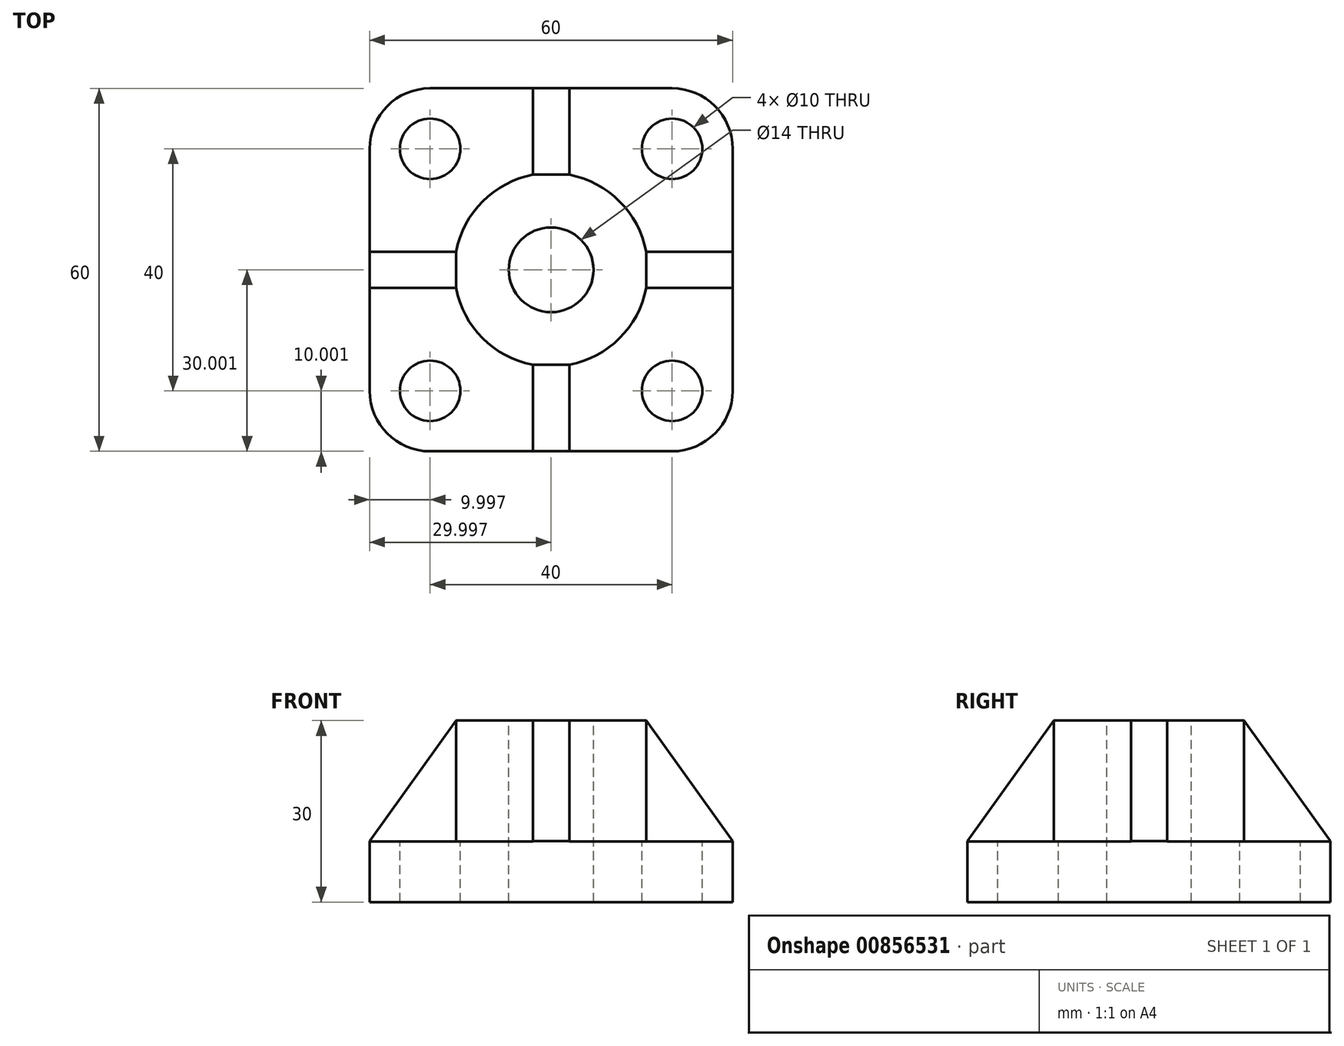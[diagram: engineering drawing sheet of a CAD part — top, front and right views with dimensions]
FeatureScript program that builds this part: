
annotation { "Feature Type Name" : "Feature", "Feature Type Description" : "" }
export const myFeature = defineFeature(function(context is Context, id is Id, definition is map)
    precondition{}
    {
        {
            var Q0;
            Q0=qCreatedBy(makeId("Top.planeOp"),FACE);
            var sketch = newSketch(context, id + "F0", { "sketchPlane" : qUnion([Q0])});
            skLineSegment(sketch, "E0.bottom", {"start": v(-13.96, 23.61) * mm, "end": v(46.04, 23.61) * mm});
            skLineSegment(sketch, "E0.top", {"start": v(-13.96, -36.39) * mm, "end": v(46.04, -36.39) * mm});
            skLineSegment(sketch, "E0.left", {"start": v(-13.96, 23.61) * mm, "end": v(-13.96, -36.39) * mm});
            skLineSegment(sketch, "E0.right", {"start": v(46.04, 23.61) * mm, "end": v(46.04, -36.39) * mm});
            skSolve(sketch);
        }
        {
            var Q0;
            Q0=makeQuery(id+"F0.imprint","IMPRINT",FACE,{"disambiguationData":[TD([[makeQuery(id+"F0.imprint","IMPRINT",EDGE,{"derivedFrom":sQuery(id+"F0.wireOp",EDGE,"E0.bottom")}),-1.0]])]});
            extrude(context, id + "F1", {"entities" : qUnion([Q0]), "depth" : 10 * mm, "offsetDistance" : 25 * mm});
        }
        {
            var Q0;
            Q0=makeQuery(id+"F1.opExtrude","SWEPT_EDGE",EDGE,{"disambiguationData":[OSD([sQuery(id+"F0.wireOp",EDGE,"E0.bottom"),sQuery(id+"F0.wireOp",EDGE,"E0.left")])]});
            var Q1;
            Q1=makeQuery(id+"F1.opExtrude","SWEPT_EDGE",EDGE,{"disambiguationData":[OSD([sQuery(id+"F0.wireOp",EDGE,"E0.bottom"),sQuery(id+"F0.wireOp",EDGE,"E0.right")])]});
            var Q2;
            Q2=makeQuery(id+"F1.opExtrude","SWEPT_EDGE",EDGE,{"disambiguationData":[OSD([sQuery(id+"F0.wireOp",EDGE,"E0.top"),sQuery(id+"F0.wireOp",EDGE,"E0.right")])]});
            var Q3;
            Q3=makeQuery(id+"F1.opExtrude","SWEPT_EDGE",EDGE,{"disambiguationData":[OSD([sQuery(id+"F0.wireOp",EDGE,"E0.top"),sQuery(id+"F0.wireOp",EDGE,"E0.left")])]});
            fillet(context, id + "F2", {"entities" : qUnion([Q0, Q1, Q2, Q3]), "radius" : 10 * mm, "tangentPropagation" : true, "allowEdgeOverflow" : false});
        }
        {
            var Q0;
            Q0=makeQuery(id+"F1.opExtrude","CAP_FACE",FACE,{"disambiguationData":[OSD([sQuery(id+"F0.wireOp",EDGE,"E0.bottom"),sQuery(id+"F0.wireOp",EDGE,"E0.top"),sQuery(id+"F0.wireOp",EDGE,"E0.left"),sQuery(id+"F0.wireOp",EDGE,"E0.right")])],"isStart":false});
            var sketch = newSketch(context, id + "F3", { "sketchPlane" : qUnion([Q0])});
            skLineSegment(sketch, "E1", {"start": v(-13.96, 13.61) * mm, "end": v(-3.96, 13.61) * mm});
            skLineSegment(sketch, "E2", {"start": v(-13.96, -26.39) * mm, "end": v(-3.96, -26.39) * mm});
            skLineSegment(sketch, "E3", {"start": v(46.04, 13.61) * mm, "end": v(36.04, 13.61) * mm});
            skLineSegment(sketch, "E4", {"start": v(46.04, -26.39) * mm, "end": v(36.04, -26.39) * mm});
            skPoint(sketch, "E5", {"position": v(16.04, -6.39) * mm});
            skCircle(sketch, "E6", {"center": v(16.04, -6.39) * mm, "radius": 16 * mm});
            skLineSegment(sketch, "E7", {"start": v(-13.96, -6.39) * mm, "end": v(-13.96, -3.39) * mm});
            skLineSegment(sketch, "E8", {"start": v(-13.96, -3.39) * mm, "end": v(0.32, -3.39) * mm});
            skLineSegment(sketch, "E9", {"start": v(-13.96, -9.39) * mm, "end": v(-13.96, -6.39) * mm});
            skLineSegment(sketch, "E10", {"start": v(16.04, -36.39) * mm, "end": v(13.04, -36.39) * mm});
            skLineSegment(sketch, "E11", {"start": v(16.04, -36.39) * mm, "end": v(19.04, -36.39) * mm});
            skLineSegment(sketch, "E12", {"start": v(13.04, -36.39) * mm, "end": v(13.04, -22.1) * mm});
            skLineSegment(sketch, "E13", {"start": v(19.04, -36.39) * mm, "end": v(19.04, -22.1) * mm});
            skLineSegment(sketch, "E14", {"start": v(46.04, -6.39) * mm, "end": v(46.04, -3.39) * mm});
            skLineSegment(sketch, "E15", {"start": v(46.04, -6.39) * mm, "end": v(46.04, -9.39) * mm});
            skLineSegment(sketch, "E16", {"start": v(46.04, -3.39) * mm, "end": v(31.75, -3.39) * mm});
            skLineSegment(sketch, "E17", {"start": v(46.04, -9.39) * mm, "end": v(31.75, -9.39) * mm});
            skLineSegment(sketch, "E18", {"start": v(16.04, 23.61) * mm, "end": v(13.04, 23.61) * mm});
            skLineSegment(sketch, "E19", {"start": v(16.04, 23.61) * mm, "end": v(19.04, 23.61) * mm});
            skLineSegment(sketch, "E20", {"start": v(13.04, 23.61) * mm, "end": v(13.04, 9.33) * mm});
            skLineSegment(sketch, "E21", {"start": v(19.04, 23.61) * mm, "end": v(19.04, 9.33) * mm});
            skLineSegment(sketch, "E22", {"start": v(-13.96, -9.39) * mm, "end": v(0.32, -9.39) * mm});
            skSolve(sketch);
        }
        {
            var Q0;
            Q0=sQuery(id+"F3.wireOp",VERTEX,"E1.end");
            var Q1;
            Q1=sQuery(id+"F3.wireOp",VERTEX,"E3.end");
            var Q2;
            Q2=sQuery(id+"F3.wireOp",VERTEX,"E4.end");
            var Q3;
            Q3=sQuery(id+"F3.wireOp",VERTEX,"E2.end");
            var Q4;
            Q4=makeQuery(id+"F1.opExtrude","SWEPT_BODY",BODY,{"disambiguationData":[OSD([sQuery(id+"F0.wireOp",EDGE,"E0.bottom"),sQuery(id+"F0.wireOp",EDGE,"E0.top"),sQuery(id+"F0.wireOp",EDGE,"E0.left"),sQuery(id+"F0.wireOp",EDGE,"E0.right")])]});
            hole(context, id + "F4", {"style" : HoleStyle.SIMPLE, "endStyle" : HoleEndStyle.THROUGH, "holeDiameter" : 10 * mm, "majorDiameter" : 16 * mm, "isTappedThrough" : true, "tappedDepth" : 25 * mm, "tapClearance" : 3, "startFromSketch" : true, "locations" : qUnion([Q0, Q1, Q2, Q3]), "scope" : qUnion([Q4])});
        }
        {
            var Q0;
            Q0 = qSketchRegion(id + "F3", true);
            extrude(context, id + "F5", {"entities" : qUnion([Q0]), "operationType" : NewBodyOperationType.ADD, "depth" : 20 * mm, "offsetDistance" : 25 * mm});
        }
        {
            var Q0;
            Q0=makeQuery(id+"F5.opExtrude","CAP_FACE",FACE,{"disambiguationData":[OSD([sQuery(id+"F3.wireOp",EDGE,"E6")])],"isStart":false});
            var sketch = newSketch(context, id + "F6", { "sketchPlane" : qUnion([Q0])});
            skPoint(sketch, "E23", {"position": v(16.04, -6.39) * mm});
            skSolve(sketch);
        }
        {
            var Q0;
            Q0=sQuery(id+"F6.wireOp",VERTEX,"E23");
            var Q1;
            Q1=makeQuery(id+"F1.opExtrude","SWEPT_BODY",BODY,{"disambiguationData":[OSD([sQuery(id+"F0.wireOp",EDGE,"E0.bottom"),sQuery(id+"F0.wireOp",EDGE,"E0.top"),sQuery(id+"F0.wireOp",EDGE,"E0.left"),sQuery(id+"F0.wireOp",EDGE,"E0.right")])]});
            hole(context, id + "F7", {"style" : HoleStyle.SIMPLE, "endStyle" : HoleEndStyle.BLIND, "standardTappedOrClearance" : lookupTablePath({ "standard" : "ISO", "engagement" : "75%", "pitch" : "2 mm", "size" : "M16", "type" : "Tapped" }), "standardBlindInLast" : lookupTablePath({ "standard" : "ISO", "engagement" : "75%", "pitch" : "2 mm", "size" : "M16", "type" : "Tapped" }), "holeDiameter" : 14 * mm, "majorDiameter" : 16 * mm, "showTappedDepth" : true, "holeDepth" : 31 * mm, "tappedDepth" : 25 * mm, "tapClearance" : 3, "startFromSketch" : true, "locations" : qUnion([Q0]), "scope" : qUnion([Q1])});
        }
        {
            var Q0;
            Q0=makeQuery(id+"F5.opExtrude","CAP_EDGE",EDGE,{"disambiguationData":[OSD([sQuery(id+"F3.wireOp",EDGE,"E7"),sQuery(id+"F3.wireOp",EDGE,"E9")])],"isStart":false});
            var Q1;
            Q1=makeQuery(id+"F5.opExtrude","CAP_EDGE",EDGE,{"disambiguationData":[OSD([sQuery(id+"F3.wireOp",EDGE,"E18"),sQuery(id+"F3.wireOp",EDGE,"E19")])],"isStart":false});
            var Q2;
            Q2=makeQuery(id+"F5.opExtrude","CAP_EDGE",EDGE,{"disambiguationData":[OSD([sQuery(id+"F3.wireOp",EDGE,"E14"),sQuery(id+"F3.wireOp",EDGE,"E15")])],"isStart":false});
            var Q3;
            Q3=makeQuery(id+"F5.opExtrude","CAP_EDGE",EDGE,{"disambiguationData":[OSD([sQuery(id+"F3.wireOp",EDGE,"E10"),sQuery(id+"F3.wireOp",EDGE,"E11")])],"isStart":false});
            chamfer(context, id + "F8", {"entities" : qUnion([Q0, Q1, Q2, Q3]), "chamferType" : ChamferType.OFFSET_ANGLE, "width" : 14.28 * mm, "oppositeDirection" : false, "angle" : 54.4 * degree, "tangentPropagation" : true});
        }
    });
